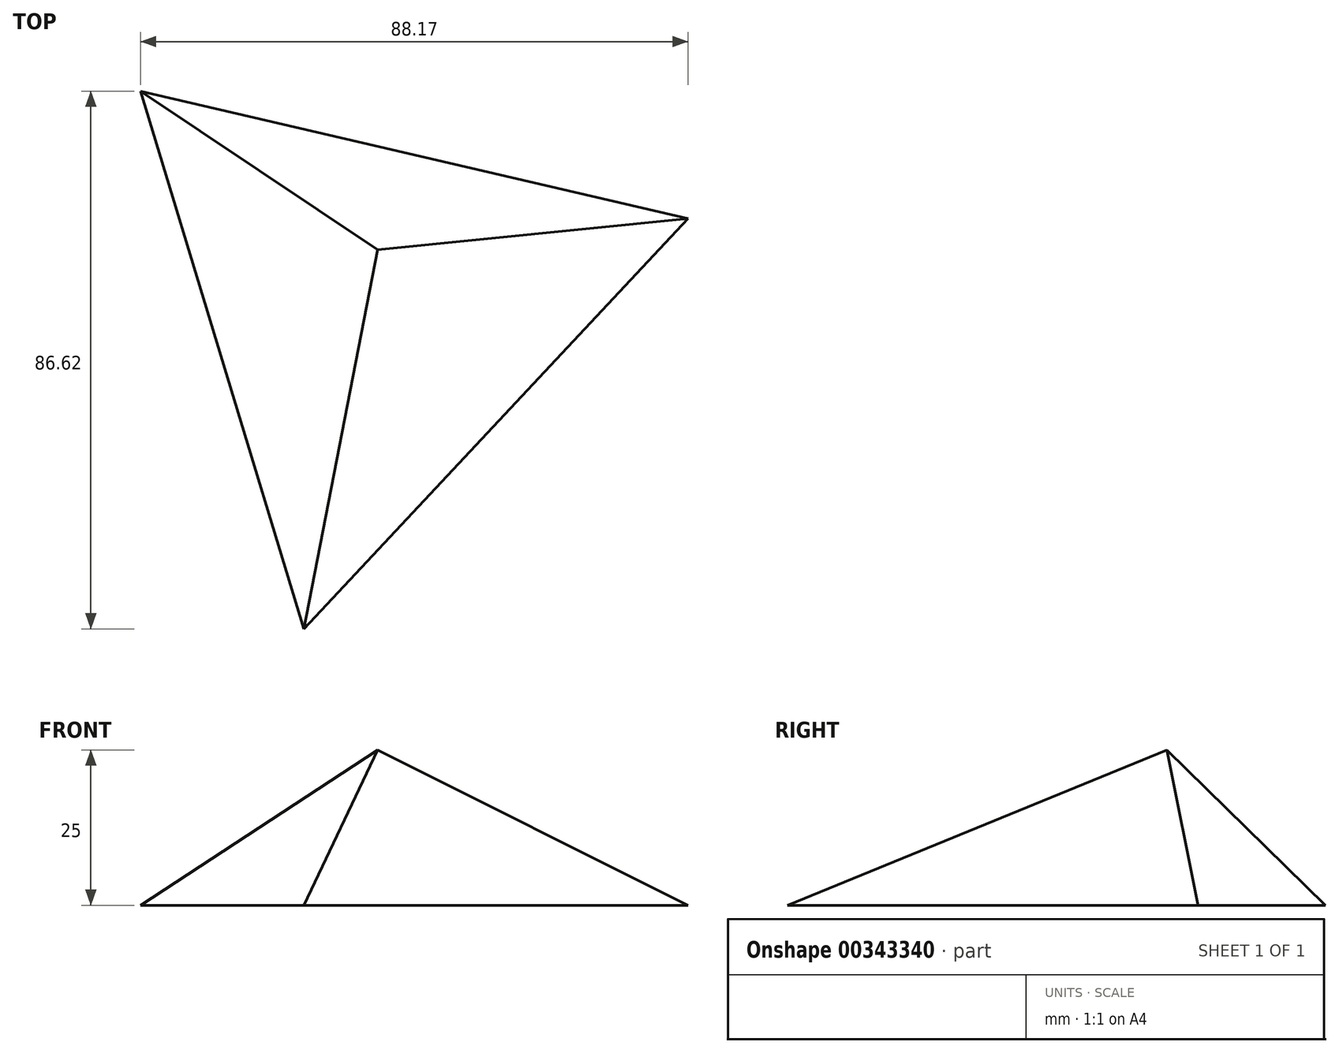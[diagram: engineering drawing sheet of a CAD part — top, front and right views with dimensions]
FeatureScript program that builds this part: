
annotation { "Feature Type Name" : "Feature", "Feature Type Description" : "" }
export const myFeature = defineFeature(function(context is Context, id is Id, definition is map)
    precondition{}
    {
        {
            var Q0;
            Q0=qCreatedBy(makeId("Top.planeOp"),FACE);
            var sketch = newSketch(context, id + "F0", { "sketchPlane" : qUnion([Q0])});
            skCircle(sketch, "E0.cCircle", {"center": v(0, 0) * mm, "radius": 52.26 * mm, "construction": true});
            skLineSegment(sketch, "E0.0", {"start": v(-38.16, 35.72) * mm, "end": v(50, 15.19) * mm});
            skLineSegment(sketch, "E0.1", {"start": v(50, 15.19) * mm, "end": v(-11.85, -50.9) * mm});
            skLineSegment(sketch, "E0.2", {"start": v(-11.85, -50.9) * mm, "end": v(-38.16, 35.72) * mm});
            skSolve(sketch);
        }
        {
            var Q0;
            Q0=qCreatedBy(makeId("Top.planeOp"),FACE);
            cPlane(context, id + "F1", {"entities" : qUnion([Q0]), "cplaneType" : CPlaneType.OFFSET, "offset" : 25 * mm, "width" : 150 * mm, "height" : 150 * mm});
        }
        {
            var Q0;
            Q0=qCreatedBy(id+"F1.planeOp",FACE);
            var sketch = newSketch(context, id + "F2", { "sketchPlane" : qUnion([Q0])});
            skLineSegment(sketch, "E1.bottom", {"start": v(48.23, -37) * mm, "end": v(-48.23, -37) * mm});
            skLineSegment(sketch, "E1.top", {"start": v(48.23, 57.36) * mm, "end": v(-48.23, 57.36) * mm});
            skLineSegment(sketch, "E1.left", {"start": v(48.23, -37) * mm, "end": v(48.23, 57.36) * mm});
            skLineSegment(sketch, "E1.right", {"start": v(-48.23, -37) * mm, "end": v(-48.23, 57.36) * mm});
            skPoint(sketch, "E1.middle", {"position": v(0, 10.17) * mm});
            skSolve(sketch);
        }
        {
            var Q0;
            Q0=sQuery(id+"F2.wireOp",VERTEX,"E1.middle");
            var Q1;
            Q1=makeQuery(id+"F0.imprint","IMPRINT",FACE,{"disambiguationData":[TD([[makeQuery(id+"F0.imprint","IMPRINT",EDGE,{"derivedFrom":sQuery(id+"F0.wireOp",EDGE,"E0.0")}),-1.0]])]});
            loft(context, id + "F3", {"sheetProfilesArray" : [{ "sheetProfileEntities" : qUnion([Q0]) }, { "sheetProfileEntities" : qUnion([Q1]) }]});
        }
    });
